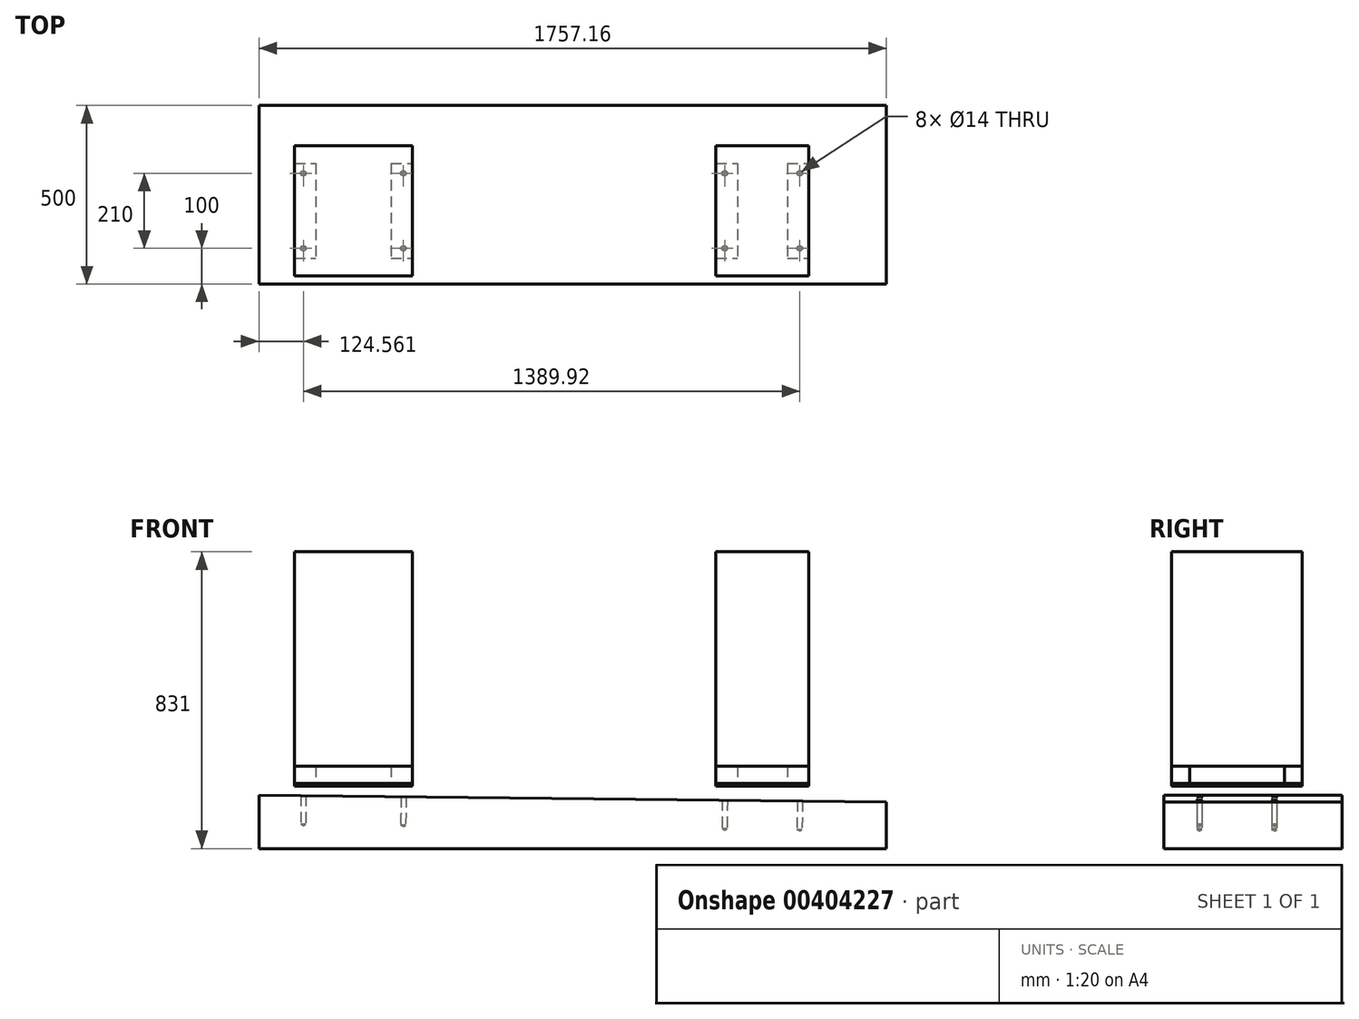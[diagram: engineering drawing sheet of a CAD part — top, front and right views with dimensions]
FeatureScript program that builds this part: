
annotation { "Feature Type Name" : "Feature", "Feature Type Description" : "" }
export const myFeature = defineFeature(function(context is Context, id is Id, definition is map)
    precondition{}
    {
        {
            var Q0;
            Q0=qCreatedBy(makeId("Front.planeOp"),FACE);
            var sketch = newSketch(context, id + "F0", { "sketchPlane" : qUnion([Q0])});
            skLineSegment(sketch, "E0", {"start": v(0, 0) * mm, "end": v(1757.16, -18.95) * mm});
            skLineSegment(sketch, "E1", {"start": v(1757.16, -18.95) * mm, "end": v(1757.16, -150) * mm});
            skLineSegment(sketch, "E2", {"start": v(1757.16, -150) * mm, "end": v(0, -150) * mm});
            skLineSegment(sketch, "E3", {"start": v(0, -150) * mm, "end": v(0, 0) * mm});
            skLineSegment(sketch, "E4", {"start": v(156.72, -1.7) * mm, "end": v(157.8, 98.3) * mm, "construction": true});
            skLineSegment(sketch, "E5", {"start": v(157.8, 98.3) * mm, "end": v(1547.8, 98.3) * mm, "construction": true});
            skLineSegment(sketch, "E6", {"start": v(1547.8, 98.3) * mm, "end": v(1547.8, -16.7) * mm, "construction": true});
            skSolve(sketch);
        }
        {
            var Q0;
            Q0=makeQuery(id+"F0.imprint","IMPRINT",FACE,{"disambiguationData":[TD([[makeQuery(id+"F0.imprint","IMPRINT",EDGE,{"derivedFrom":sQuery(id+"F0.wireOp",EDGE,"E0")}),-1.0]])]});
            extrude(context, id + "F1", {"entities" : qUnion([Q0]), "oppositeDirection" : true, "depth" : 500 * mm, "offsetDistance" : 25 * mm});
        }
        {
            var Q0;
            Q0=makeQuery(id+"F1.opExtrude","SWEPT_FACE",FACE,{"disambiguationData":[OSD([sQuery(id+"F0.wireOp",EDGE,"E0")])]});
            var sketch = newSketch(context, id + "F2", { "sketchPlane" : qUnion([Q0])});
            skPoint(sketch, "E7", {"position": v(125, 100) * mm});
            skPoint(sketch, "E8", {"position": v(125, 310) * mm});
            skPoint(sketch, "E9", {"position": v(405, 310) * mm});
            skPoint(sketch, "E10", {"position": v(405, 100) * mm});
            skPoint(sketch, "E11", {"position": v(1305, 310) * mm});
            skPoint(sketch, "E12", {"position": v(1305, 100) * mm});
            skPoint(sketch, "E13", {"position": v(1515, 100) * mm});
            skPoint(sketch, "E14", {"position": v(1515, 310) * mm});
            skSolve(sketch);
        }
        {
            var Q0;
            Q0=sQuery(id+"F2.wireOp",VERTEX,"E8");
            var Q1;
            Q1=sQuery(id+"F2.wireOp",VERTEX,"E7");
            var Q2;
            Q2=sQuery(id+"F2.wireOp",VERTEX,"E10");
            var Q3;
            Q3=sQuery(id+"F2.wireOp",VERTEX,"E9");
            var Q4;
            Q4=sQuery(id+"F2.wireOp",VERTEX,"E12");
            var Q5;
            Q5=sQuery(id+"F2.wireOp",VERTEX,"E13");
            var Q6;
            Q6=sQuery(id+"F2.wireOp",VERTEX,"E14");
            var Q7;
            Q7=sQuery(id+"F2.wireOp",VERTEX,"E11");
            var Q8;
            Q8=makeQuery(id+"F1.opExtrude","SWEPT_BODY",BODY,{"disambiguationData":[OSD([sQuery(id+"F0.wireOp",EDGE,"E0"),sQuery(id+"F0.wireOp",EDGE,"E1"),sQuery(id+"F0.wireOp",EDGE,"E2"),sQuery(id+"F0.wireOp",EDGE,"E3")])]});
            hole(context, id + "F3", {"style" : HoleStyle.SIMPLE, "endStyle" : HoleEndStyle.BLIND, "standardTappedOrClearance" : lookupTablePath({ "standard" : "ISO", "size" : "14", "type" : "Drilled" }), "standardBlindInLast" : lookupTablePath({ "standard" : "ISO", "size" : "14", "type" : "Drilled" }), "holeDiameter" : 14 * mm, "majorDiameter" : 5 * mm, "holeDepth" : 80 * mm, "isTappedThrough" : true, "tappedDepth" : 11.2 * mm, "tapClearance" : 3, "startFromSketch" : true, "locations" : qUnion([Q0, Q1, Q2, Q3, Q4, Q5, Q6, Q7]), "scope" : qUnion([Q8])});
        }
        {
            var Q0;
            Q0=makeQuery(id+"F1.opExtrude","SWEPT_FACE",FACE,{"disambiguationData":[OSD([sQuery(id+"F0.wireOp",EDGE,"E2")])]});
            cPlane(context, id + "F4", {"entities" : qUnion([Q0]), "cplaneType" : CPlaneType.OFFSET, "offset" : 175 * mm, "oppositeDirection" : true, "width" : 150 * mm, "height" : 150 * mm});
        }
        {
            var Q0;
            Q0=qCreatedBy(id+"F4.planeOp",FACE);
            var sketch = newSketch(context, id + "F5", { "sketchPlane" : qUnion([Q0])});
            skLineSegment(sketch, "E15.bottom", {"start": v(100, -387.5) * mm, "end": v(430, -387.5) * mm});
            skLineSegment(sketch, "E15.top", {"start": v(100, -22.5) * mm, "end": v(430, -22.5) * mm});
            skLineSegment(sketch, "E15.left", {"start": v(100, -387.5) * mm, "end": v(100, -22.5) * mm});
            skLineSegment(sketch, "E15.right", {"start": v(430, -387.5) * mm, "end": v(430, -22.5) * mm});
            skLineSegment(sketch, "E16.bottom", {"start": v(1279.92, -387.5) * mm, "end": v(1539.92, -387.5) * mm});
            skLineSegment(sketch, "E16.top", {"start": v(1279.92, -22.5) * mm, "end": v(1539.92, -22.5) * mm});
            skLineSegment(sketch, "E16.left", {"start": v(1279.92, -387.5) * mm, "end": v(1279.92, -22.5) * mm});
            skLineSegment(sketch, "E16.right", {"start": v(1539.92, -387.5) * mm, "end": v(1539.92, -22.5) * mm});
            skSolve(sketch);
        }
        {
            var Q0;
            Q0=makeQuery(id+"F5.imprint","IMPRINT",FACE,{"disambiguationData":[TD([[makeQuery(id+"F5.imprint","IMPRINT",EDGE,{"derivedFrom":sQuery(id+"F5.wireOp",EDGE,"E15.bottom")}),1.0]])]});
            var Q1;
            Q1=makeQuery(id+"F5.imprint","IMPRINT",FACE,{"disambiguationData":[TD([[makeQuery(id+"F5.imprint","IMPRINT",EDGE,{"derivedFrom":sQuery(id+"F5.wireOp",EDGE,"E16.bottom")}),1.0]])]});
            extrude(context, id + "F6", {"entities" : qUnion([Q0, Q1]), "oppositeDirection" : true, "depth" : 8 * mm, "offsetDistance" : 25 * mm});
        }
        {
            var Q0;
            Q0=makeQuery(id+"F6.opExtrude","CAP_FACE",FACE,{"disambiguationData":[OSD([sQuery(id+"F5.wireOp",EDGE,"E15.bottom"),sQuery(id+"F5.wireOp",EDGE,"E15.top"),sQuery(id+"F5.wireOp",EDGE,"E15.left"),sQuery(id+"F5.wireOp",EDGE,"E15.right")])],"isStart":false});
            var sketch = newSketch(context, id + "F7", { "sketchPlane" : qUnion([Q0])});
            skLineSegment(sketch, "E17", {"start": v(100, 337.5) * mm, "end": v(160, 337.5) * mm});
            skLineSegment(sketch, "E18", {"start": v(100, 72.5) * mm, "end": v(160, 72.5) * mm});
            skLineSegment(sketch, "E19", {"start": v(160, 337.5) * mm, "end": v(160, 72.5) * mm});
            skLineSegment(sketch, "E20", {"start": v(370, 337.5) * mm, "end": v(370, 72.5) * mm});
            skLineSegment(sketch, "E21.trimOffspring", {"start": v(370, 337.5) * mm, "end": v(430, 337.5) * mm});
            skLineSegment(sketch, "E22.trimOffspring", {"start": v(370, 72.5) * mm, "end": v(430, 72.5) * mm});
            skPoint(sketch, "E23.startSnap0", {"position": v(400, 72.5) * mm});
            skSolve(sketch);
        }
        {
            var Q0;
            Q0=makeQuery(id+"F6.opExtrude","CAP_FACE",FACE,{"disambiguationData":[OSD([sQuery(id+"F5.wireOp",EDGE,"E16.bottom"),sQuery(id+"F5.wireOp",EDGE,"E16.top"),sQuery(id+"F5.wireOp",EDGE,"E16.left"),sQuery(id+"F5.wireOp",EDGE,"E16.right")])],"isStart":false});
            var sketch = newSketch(context, id + "F8", { "sketchPlane" : qUnion([Q0])});
            skLineSegment(sketch, "E24", {"start": v(1279.92, 337.5) * mm, "end": v(1339.92, 337.5) * mm});
            skLineSegment(sketch, "E25", {"start": v(1279.92, 72.5) * mm, "end": v(1339.92, 72.5) * mm});
            skLineSegment(sketch, "E26", {"start": v(1339.92, 337.5) * mm, "end": v(1339.92, 72.5) * mm});
            skLineSegment(sketch, "E27", {"start": v(1479.92, 337.5) * mm, "end": v(1479.92, 72.5) * mm});
            skLineSegment(sketch, "E28.trimOffspring", {"start": v(1479.92, 337.5) * mm, "end": v(1539.92, 337.5) * mm});
            skLineSegment(sketch, "E29.trimOffspring", {"start": v(1479.92, 72.5) * mm, "end": v(1539.92, 72.5) * mm});
            skSolve(sketch);
        }
        {
            var Q0;
            {var subQ4=sQuery(id+"F8.wireOp",EDGE,"E24");Q0=makeQuery(id+"F8.imprint","IMPRINT",FACE,{"disambiguationData":[TD([[makeQuery(id+"F8.imprint","IMPRINT",EDGE,{"derivedFrom":subQ4}),1.0]])]});}
            var Q1;
            {var subQ4=sQuery(id+"F7.wireOp",EDGE,"E17");Q1=makeQuery(id+"F7.imprint","IMPRINT",FACE,{"disambiguationData":[TD([[makeQuery(id+"F7.imprint","IMPRINT",EDGE,{"derivedFrom":subQ4}),1.0]])]});}
            extrude(context, id + "F9", {"entities" : qUnion([Q0, Q1]), "depth" : 48 * mm, "offsetDistance" : 25 * mm});
        }
        {
            var Q0;
            Q0=makeQuery(id+"F9.opExtrude","CAP_FACE",FACE,{"disambiguationData":[OSD([sQuery(id+"F5.wireOp",EDGE,"E15.bottom"),sQuery(id+"F5.wireOp",EDGE,"E15.top"),sQuery(id+"F5.wireOp",EDGE,"E15.left"),sQuery(id+"F5.wireOp",EDGE,"E15.right"),sQuery(id+"F7.wireOp",EDGE,"E17"),sQuery(id+"F7.wireOp",EDGE,"E18"),sQuery(id+"F7.wireOp",EDGE,"E19"),sQuery(id+"F7.wireOp",EDGE,"E20"),sQuery(id+"F7.wireOp",EDGE,"E21.trimOffspring"),sQuery(id+"F7.wireOp",EDGE,"E22.trimOffspring")])],"isStart":false});
            var sketch = newSketch(context, id + "F10", { "sketchPlane" : qUnion([Q0])});
            skLineSegment(sketch, "E30.bottom", {"start": v(100, 387.5) * mm, "end": v(430, 387.5) * mm});
            skLineSegment(sketch, "E30.top", {"start": v(100, 22.5) * mm, "end": v(430, 22.5) * mm});
            skLineSegment(sketch, "E30.left", {"start": v(100, 387.5) * mm, "end": v(100, 22.5) * mm});
            skLineSegment(sketch, "E30.right", {"start": v(430, 387.5) * mm, "end": v(430, 22.5) * mm});
            skSolve(sketch);
        }
        {
            var Q0;
            Q0=makeQuery(id+"F9.opExtrude","CAP_FACE",FACE,{"disambiguationData":[OSD([sQuery(id+"F5.wireOp",EDGE,"E16.bottom"),sQuery(id+"F5.wireOp",EDGE,"E16.top"),sQuery(id+"F5.wireOp",EDGE,"E16.left"),sQuery(id+"F5.wireOp",EDGE,"E16.right"),sQuery(id+"F8.wireOp",EDGE,"E24"),sQuery(id+"F8.wireOp",EDGE,"E25"),sQuery(id+"F8.wireOp",EDGE,"E26"),sQuery(id+"F8.wireOp",EDGE,"E27"),sQuery(id+"F8.wireOp",EDGE,"E28.trimOffspring"),sQuery(id+"F8.wireOp",EDGE,"E29.trimOffspring")])],"isStart":false});
            var sketch = newSketch(context, id + "F11", { "sketchPlane" : qUnion([Q0])});
            skLineSegment(sketch, "E31.bottom", {"start": v(1279.92, 387.5) * mm, "end": v(1539.92, 387.5) * mm});
            skLineSegment(sketch, "E31.top", {"start": v(1279.92, 22.5) * mm, "end": v(1539.92, 22.5) * mm});
            skLineSegment(sketch, "E31.left", {"start": v(1279.92, 387.5) * mm, "end": v(1279.92, 22.5) * mm});
            skLineSegment(sketch, "E31.right", {"start": v(1539.92, 387.5) * mm, "end": v(1539.92, 22.5) * mm});
            skSolve(sketch);
        }
        {
            var Q0;
            Q0 = qSketchRegion(id + "F11", true);
            var Q1;
            Q1 = qSketchRegion(id + "F10", true);
            extrude(context, id + "F12", {"entities" : qUnion([Q0, Q1]), "depth" : 600 * mm, "offsetDistance" : 25 * mm});
        }
    });
